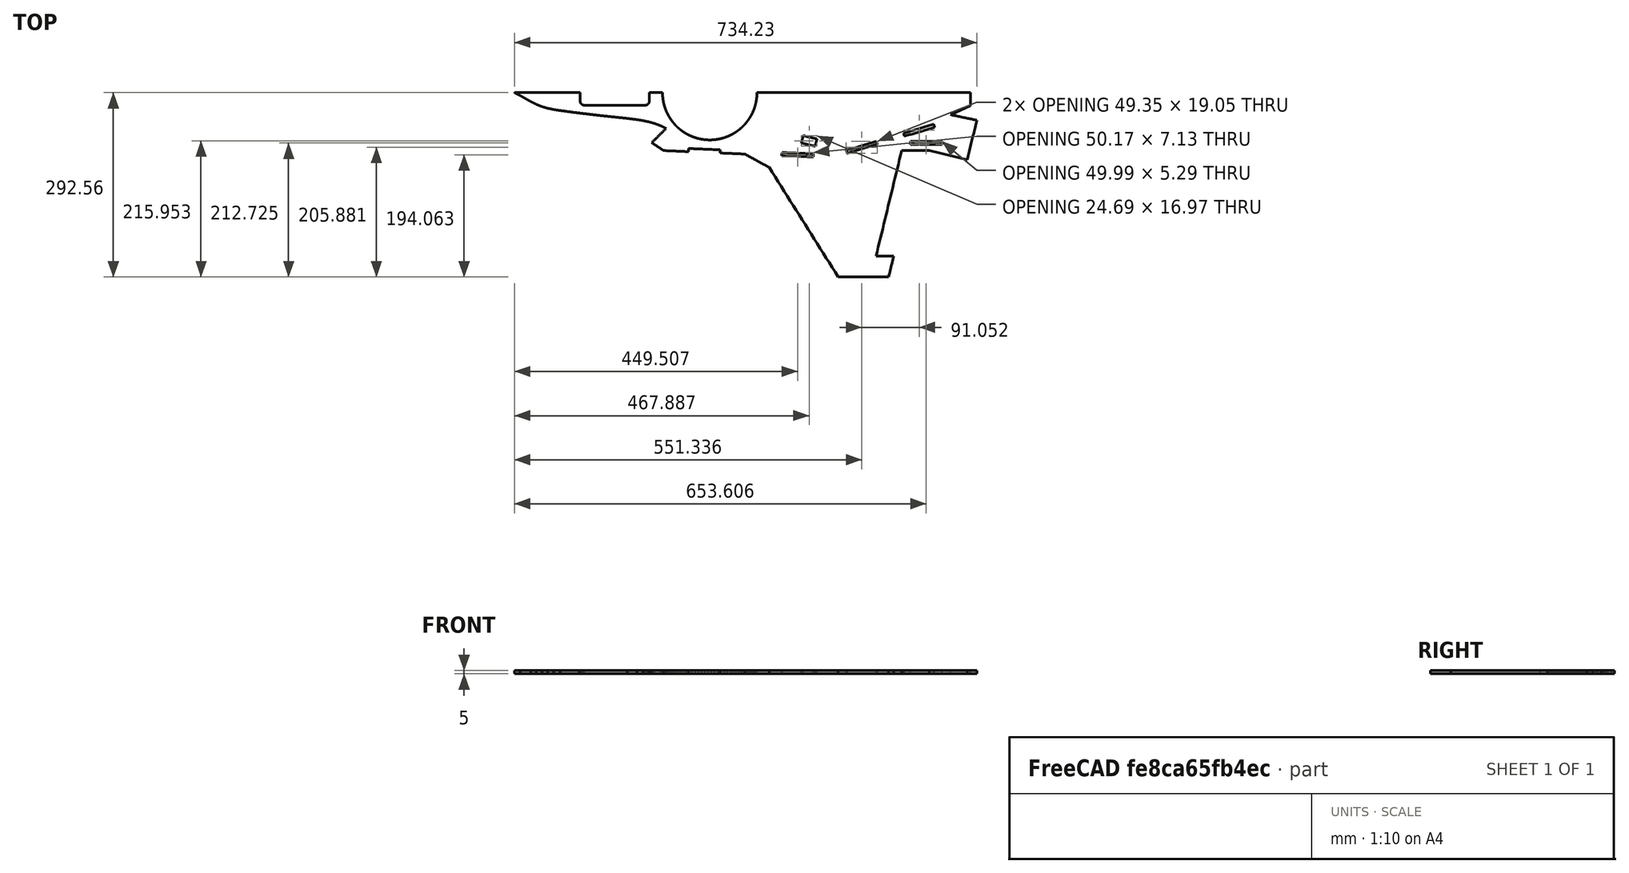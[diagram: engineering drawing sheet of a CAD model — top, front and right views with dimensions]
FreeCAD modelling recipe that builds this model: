
FCSTD DOCUMENT  (FreeCAD 0.19R)
Label: F-35_v2_parts_1
License: All rights reserved
LicenseURL: http://en.wikipedia.org/wiki/All_rights_reserved
objects: PartDesign::CoordinateSystem×8, App::DocumentObjectGroup×2, App::FeaturePython×1, Sketcher::SketchObject×1, PartDesign::Pad×1, PartDesign::Body×1, App::Part×1
note: 12 computed .brp shape members not serialized (recipe doc carries the construction recipe); baked Part::Feature solids carry a one-line shape summary decoded from their .brp

FEATURE [App::DocumentObjectGroup] Parts
FEATURE [PartDesign::CoordinateSystem] LCS_Origin
  AttacherType = Attacher::AttachEngine3D
  MapMode = 2
  Support = -> [X_Axis]
FEATURE [App::DocumentObjectGroup] Constraints
FEATURE [App::FeaturePython] Variables  # WARN: FeaturePython — macro-defined, semantics opaque (R4)
FEATURE [Sketcher::SketchObject] Sketch
  FullyConstrained = false
  sketch-geometry (125):
    g0: BSplineCurve PolesCount=2 KnotsCount=2 Degree=1 IsPeriodic=0
    g1: BSplineCurve PolesCount=2 KnotsCount=2 Degree=1 IsPeriodic=0
    g2: BSplineCurve PolesCount=2 KnotsCount=2 Degree=1 IsPeriodic=0
    g3: BSplineCurve PolesCount=2 KnotsCount=2 Degree=1 IsPeriodic=0
    g4: BSplineCurve PolesCount=2 KnotsCount=2 Degree=1 IsPeriodic=0
    g5: BSplineCurve PolesCount=2 KnotsCount=2 Degree=1 IsPeriodic=0
    g6: BSplineCurve PolesCount=2 KnotsCount=2 Degree=1 IsPeriodic=0
    g7: BSplineCurve PolesCount=2 KnotsCount=2 Degree=1 IsPeriodic=0
    g8: BSplineCurve PolesCount=2 KnotsCount=2 Degree=1 IsPeriodic=0
    g9: BSplineCurve PolesCount=2 KnotsCount=2 Degree=1 IsPeriodic=0
    g10: BSplineCurve PolesCount=2 KnotsCount=2 Degree=1 IsPeriodic=0
    g11: BSplineCurve PolesCount=2 KnotsCount=2 Degree=1 IsPeriodic=0
    g12: BSplineCurve PolesCount=2 KnotsCount=2 Degree=1 IsPeriodic=0
    g13: BSplineCurve PolesCount=2 KnotsCount=2 Degree=1 IsPeriodic=0
    g14: BSplineCurve PolesCount=2 KnotsCount=2 Degree=1 IsPeriodic=0
    g15: BSplineCurve PolesCount=2 KnotsCount=2 Degree=1 IsPeriodic=0
    g16: BSplineCurve PolesCount=2 KnotsCount=2 Degree=1 IsPeriodic=0
    g17: BSplineCurve PolesCount=2 KnotsCount=2 Degree=1 IsPeriodic=0
    g18: BSplineCurve PolesCount=2 KnotsCount=2 Degree=1 IsPeriodic=0
    g19: BSplineCurve PolesCount=2 KnotsCount=2 Degree=1 IsPeriodic=0
    g20: BSplineCurve PolesCount=2 KnotsCount=2 Degree=1 IsPeriodic=0
    g21: BSplineCurve PolesCount=2 KnotsCount=2 Degree=1 IsPeriodic=0
    g22: BSplineCurve PolesCount=2 KnotsCount=2 Degree=1 IsPeriodic=0
    g23: BSplineCurve PolesCount=2 KnotsCount=2 Degree=1 IsPeriodic=0
    g24: BSplineCurve PolesCount=2 KnotsCount=2 Degree=1 IsPeriodic=0
    g25: BSplineCurve PolesCount=2 KnotsCount=2 Degree=1 IsPeriodic=0
    g26: BSplineCurve PolesCount=2 KnotsCount=2 Degree=1 IsPeriodic=0
    g27: BSplineCurve PolesCount=2 KnotsCount=2 Degree=1 IsPeriodic=0
    g28: BSplineCurve PolesCount=2 KnotsCount=2 Degree=1 IsPeriodic=0
    g29: BSplineCurve PolesCount=2 KnotsCount=2 Degree=1 IsPeriodic=0
    g30: BSplineCurve PolesCount=2 KnotsCount=2 Degree=1 IsPeriodic=0
    g31: BSplineCurve PolesCount=2 KnotsCount=2 Degree=1 IsPeriodic=0
    g32: BSplineCurve PolesCount=2 KnotsCount=2 Degree=1 IsPeriodic=0
    g33: BSplineCurve PolesCount=2 KnotsCount=2 Degree=1 IsPeriodic=0
    g34: BSplineCurve PolesCount=2 KnotsCount=2 Degree=1 IsPeriodic=0
    g35: BSplineCurve PolesCount=2 KnotsCount=2 Degree=1 IsPeriodic=0
    g36: BSplineCurve PolesCount=2 KnotsCount=2 Degree=1 IsPeriodic=0
    g37: BSplineCurve PolesCount=2 KnotsCount=2 Degree=1 IsPeriodic=0
    g38: BSplineCurve PolesCount=2 KnotsCount=2 Degree=1 IsPeriodic=0
    g39: BSplineCurve PolesCount=2 KnotsCount=2 Degree=1 IsPeriodic=0
    g40: BSplineCurve PolesCount=2 KnotsCount=2 Degree=1 IsPeriodic=0
    g41: BSplineCurve PolesCount=2 KnotsCount=2 Degree=1 IsPeriodic=0
    g42: BSplineCurve PolesCount=2 KnotsCount=2 Degree=1 IsPeriodic=0
    g43: BSplineCurve PolesCount=2 KnotsCount=2 Degree=1 IsPeriodic=0
    g44: BSplineCurve PolesCount=2 KnotsCount=2 Degree=1 IsPeriodic=0
    g45: BSplineCurve PolesCount=2 KnotsCount=2 Degree=1 IsPeriodic=0
    g46: BSplineCurve PolesCount=2 KnotsCount=2 Degree=1 IsPeriodic=0
    g47: BSplineCurve PolesCount=2 KnotsCount=2 Degree=1 IsPeriodic=0
    g48: BSplineCurve PolesCount=2 KnotsCount=2 Degree=1 IsPeriodic=0
    g49: BSplineCurve PolesCount=2 KnotsCount=2 Degree=1 IsPeriodic=0
    g50: BSplineCurve PolesCount=2 KnotsCount=2 Degree=1 IsPeriodic=0
    g51: BSplineCurve PolesCount=2 KnotsCount=2 Degree=1 IsPeriodic=0
    g52: BSplineCurve PolesCount=2 KnotsCount=2 Degree=1 IsPeriodic=0
    g53: BSplineCurve PolesCount=2 KnotsCount=2 Degree=1 IsPeriodic=0
    g54: BSplineCurve PolesCount=2 KnotsCount=2 Degree=1 IsPeriodic=0
    g55: BSplineCurve PolesCount=2 KnotsCount=2 Degree=1 IsPeriodic=0
    g56: BSplineCurve PolesCount=2 KnotsCount=2 Degree=1 IsPeriodic=0
    g57: BSplineCurve PolesCount=2 KnotsCount=2 Degree=1 IsPeriodic=0
    g58: BSplineCurve PolesCount=2 KnotsCount=2 Degree=1 IsPeriodic=0
    g59: BSplineCurve PolesCount=2 KnotsCount=2 Degree=1 IsPeriodic=0
    g60: BSplineCurve PolesCount=2 KnotsCount=2 Degree=1 IsPeriodic=0
    g61: BSplineCurve PolesCount=2 KnotsCount=2 Degree=1 IsPeriodic=0
    g62: BSplineCurve PolesCount=2 KnotsCount=2 Degree=1 IsPeriodic=0
    g63: BSplineCurve PolesCount=2 KnotsCount=2 Degree=1 IsPeriodic=0
    g64: BSplineCurve PolesCount=2 KnotsCount=2 Degree=1 IsPeriodic=0
    g65: BSplineCurve PolesCount=2 KnotsCount=2 Degree=1 IsPeriodic=0
    g66: BSplineCurve PolesCount=2 KnotsCount=2 Degree=1 IsPeriodic=0
    g67: BSplineCurve PolesCount=2 KnotsCount=2 Degree=1 IsPeriodic=0
    g68: BSplineCurve PolesCount=2 KnotsCount=2 Degree=1 IsPeriodic=0
    g69: BSplineCurve PolesCount=2 KnotsCount=2 Degree=1 IsPeriodic=0
    g70: BSplineCurve PolesCount=2 KnotsCount=2 Degree=1 IsPeriodic=0
    g71: BSplineCurve PolesCount=2 KnotsCount=2 Degree=1 IsPeriodic=0
    g72: BSplineCurve PolesCount=2 KnotsCount=2 Degree=1 IsPeriodic=0
    g73: BSplineCurve PolesCount=2 KnotsCount=2 Degree=1 IsPeriodic=0
    g74: BSplineCurve PolesCount=2 KnotsCount=2 Degree=1 IsPeriodic=0
    g75: BSplineCurve PolesCount=2 KnotsCount=2 Degree=1 IsPeriodic=0
    g76: BSplineCurve PolesCount=2 KnotsCount=2 Degree=1 IsPeriodic=0
    g77: BSplineCurve PolesCount=2 KnotsCount=2 Degree=1 IsPeriodic=0
    g78: BSplineCurve PolesCount=2 KnotsCount=2 Degree=1 IsPeriodic=0
    g79: BSplineCurve PolesCount=2 KnotsCount=2 Degree=1 IsPeriodic=0
    g80: BSplineCurve PolesCount=2 KnotsCount=2 Degree=1 IsPeriodic=0
    g81: BSplineCurve PolesCount=2 KnotsCount=2 Degree=1 IsPeriodic=0
    g82: BSplineCurve PolesCount=2 KnotsCount=2 Degree=1 IsPeriodic=0
    g83: BSplineCurve PolesCount=2 KnotsCount=2 Degree=1 IsPeriodic=0
    g84: BSplineCurve PolesCount=2 KnotsCount=2 Degree=1 IsPeriodic=0
    g85: BSplineCurve PolesCount=2 KnotsCount=2 Degree=1 IsPeriodic=0
    g86: BSplineCurve PolesCount=2 KnotsCount=2 Degree=1 IsPeriodic=0
    g87: BSplineCurve PolesCount=2 KnotsCount=2 Degree=1 IsPeriodic=0
    g88: BSplineCurve PolesCount=2 KnotsCount=2 Degree=1 IsPeriodic=0
    g89: BSplineCurve PolesCount=2 KnotsCount=2 Degree=1 IsPeriodic=0
    g90: BSplineCurve PolesCount=2 KnotsCount=2 Degree=1 IsPeriodic=0
    g91: BSplineCurve PolesCount=2 KnotsCount=2 Degree=1 IsPeriodic=0
    g92: BSplineCurve PolesCount=2 KnotsCount=2 Degree=1 IsPeriodic=0
    g93: BSplineCurve PolesCount=2 KnotsCount=2 Degree=1 IsPeriodic=0
    g94: BSplineCurve PolesCount=2 KnotsCount=2 Degree=1 IsPeriodic=0
    g95: BSplineCurve PolesCount=2 KnotsCount=2 Degree=1 IsPeriodic=0
    g96: BSplineCurve PolesCount=2 KnotsCount=2 Degree=1 IsPeriodic=0
    g97: BSplineCurve PolesCount=2 KnotsCount=2 Degree=1 IsPeriodic=0
    g98: BSplineCurve PolesCount=2 KnotsCount=2 Degree=1 IsPeriodic=0
    g99: BSplineCurve PolesCount=2 KnotsCount=2 Degree=1 IsPeriodic=0
    g100: BSplineCurve PolesCount=2 KnotsCount=2 Degree=1 IsPeriodic=0
    g101: BSplineCurve PolesCount=2 KnotsCount=2 Degree=1 IsPeriodic=0
    g102: BSplineCurve PolesCount=2 KnotsCount=2 Degree=1 IsPeriodic=0
    g103: BSplineCurve PolesCount=2 KnotsCount=2 Degree=1 IsPeriodic=0
    g104: BSplineCurve PolesCount=2 KnotsCount=2 Degree=1 IsPeriodic=0
    g105: BSplineCurve PolesCount=2 KnotsCount=2 Degree=1 IsPeriodic=0
    g106: BSplineCurve PolesCount=2 KnotsCount=2 Degree=1 IsPeriodic=0
    g107: BSplineCurve PolesCount=2 KnotsCount=2 Degree=1 IsPeriodic=0
    g108: BSplineCurve PolesCount=2 KnotsCount=2 Degree=1 IsPeriodic=0
    g109: BSplineCurve PolesCount=2 KnotsCount=2 Degree=1 IsPeriodic=0
    g110: BSplineCurve PolesCount=2 KnotsCount=2 Degree=1 IsPeriodic=0
    g111: BSplineCurve PolesCount=2 KnotsCount=2 Degree=1 IsPeriodic=0
    g112: BSplineCurve PolesCount=2 KnotsCount=2 Degree=1 IsPeriodic=0
    g113: BSplineCurve PolesCount=2 KnotsCount=2 Degree=1 IsPeriodic=0
    g114: BSplineCurve PolesCount=2 KnotsCount=2 Degree=1 IsPeriodic=0
    g115: BSplineCurve PolesCount=2 KnotsCount=2 Degree=1 IsPeriodic=0
    g116: BSplineCurve PolesCount=2 KnotsCount=2 Degree=1 IsPeriodic=0
    g117: BSplineCurve PolesCount=2 KnotsCount=2 Degree=1 IsPeriodic=0
    g118: BSplineCurve PolesCount=2 KnotsCount=2 Degree=1 IsPeriodic=0
    g119: BSplineCurve PolesCount=2 KnotsCount=2 Degree=1 IsPeriodic=0
    g120: BSplineCurve PolesCount=2 KnotsCount=2 Degree=1 IsPeriodic=0
    g121: BSplineCurve PolesCount=2 KnotsCount=2 Degree=1 IsPeriodic=0
    g122: BSplineCurve PolesCount=2 KnotsCount=2 Degree=1 IsPeriodic=0
    g123: BSplineCurve PolesCount=2 KnotsCount=2 Degree=1 IsPeriodic=0
    g124: BSplineCurve PolesCount=2 KnotsCount=2 Degree=1 IsPeriodic=0
  constraints (76):
    c: Coincident(g20,g21)
    c: Coincident(g21,g22)
    c: Coincident(g22,g23)
    c: Coincident(g23,g24)
    c: Coincident(g24,g25)
    c: Coincident(g25,g26)
    c: Coincident(g26,g27)
    c: Coincident(g29,g30)
    c: Coincident(g30,g31)
    c: Coincident(g31,g32)
    c: Coincident(g32,g33)
    c: Coincident(g33,g34)
    c: Coincident(g34,g35)
    c: Coincident(g35,g36)
    c: Coincident(g39,g40)
    c: Coincident(g40,g41)
    c: Coincident(g41,g42)
    c: Coincident(g42,g43)
    c: Coincident(g43,g44)
    c: Coincident(g44,g45)
    c: Coincident(g45,g46)
    c: Coincident(g46,g47)
    c: Coincident(g47,g48)
    c: Coincident(g48,g49)
    c: Coincident(g49,g50)
    c: Coincident(g50,g51)
    c: Coincident(g51,g52)
    c: Coincident(g52,g53)
    c: Coincident(g53,g54)
    c: Coincident(g54,g55)
    c: Coincident(g55,g56)
    c: Coincident(g56,g57)
    c: Coincident(g57,g58)
    c: Coincident(g58,g59)
    c: Coincident(g59,g60)
    c: Coincident(g60,g61)
    c: Coincident(g61,g62)
    c: Coincident(g62,g63)
    c: Coincident(g63,g64)
    c: Coincident(g64,g65)
    c: Coincident(g65,g66)
    c: Coincident(g66,g67)
    c: Coincident(g67,g68)
    c: Coincident(g68,g69)
    c: Coincident(g69,g70)
    c: Coincident(g70,g71)
    c: Coincident(g71,g72)
    c: Coincident(g72,g73)
    c: Coincident(g73,g74)
    c: Coincident(g74,g75)
    c: Coincident(g75,g76)
    c: Coincident(g76,g77)
    c: Coincident(g77,g78)
    c: Coincident(g78,g79)
    c: Coincident(g79,g80)
    c: Coincident(g80,g81)
    c: Coincident(g81,g82)
    c: Coincident(g82,g83)
    c: Coincident(g103,g104)
    c: Coincident(g104,g105)
    c: Coincident(g105,g106)
    c: Coincident(g106,g107)
    c: Coincident(g107,g108)
    c: Coincident(g108,g109)
    c: Coincident(g109,g110)
    c: Coincident(g110,g111)
    c: Coincident(g111,g112)
    c: Coincident(g112,g113)
    c: Coincident(g113,g114)
    c: Coincident(g114,g115)
    c: Coincident(g115,g116)
    c: Coincident(g116,g117)
    c: Coincident(g117,g118)
    c: Coincident(g118,g119)
    c: Coincident(g119,g120)
    c: Coincident(g120,g121)
FEATURE [PartDesign::Pad] Pad
  Direction = (1,1,1)
  Length = 5
  Length2 = 100
  Profile = -> Sketch
  Type = 0
FEATURE [PartDesign::Body] Body  label="Part1"
  Group = -> [Sketch,Pad]
  Origin = -> Origin001
  Tip = -> Pad
FEATURE [PartDesign::CoordinateSystem] LCS_1
  AttacherType = Attacher::AttachEngine3D
  MapMode = 7
  Placement = pos=(856.063,-121.302,0) rot=(0,1,0;3.14159rad)
  Support = -> [Pad]
FEATURE [PartDesign::CoordinateSystem] LCS_2
  AttacherType = Attacher::AttachEngine3D
  MapMode = 7
  Placement = pos=(367.078,-121.302,0) rot=(0,1,0;3.14159rad)
  Support = -> [Pad]
FEATURE [PartDesign::CoordinateSystem] LCS_3
  AttacherType = Attacher::AttachEngine3D
  MapMode = 7
  Placement = pos=(408.529,-209.884,0) rot=(0.014931,0.707028,0.707028;3.11173rad)
  Support = -> [Pad]
FEATURE [PartDesign::CoordinateSystem] LCS_4
  AttacherType = Attacher::AttachEngine3D
  MapMode = 7
  Placement = pos=(658.719,-212.706,0) rot=(-0.101306,0.703469,0.703469;3.34352rad)
  Support = -> [Pad]
FEATURE [PartDesign::CoordinateSystem] LCS_6
  AttacherType = Attacher::AttachEngine3D
  MapMode = 7
  Placement = pos=(850.63,-227.699,5) rot=(0.985165,-0.121346,-0.121346;1.58574rad)
  Support = -> [Pad]
FEATURE [PartDesign::CoordinateSystem] LCS_5
  AttacherType = Attacher::AttachEngine3D
  MapMode = 7
  Placement = pos=(746.737,-213.2,5) rot=(0.084189,0.704596,0.704596;2.97361rad)
  Support = -> [Pad]
FEATURE [PartDesign::CoordinateSystem] LCS_7
  AttacherType = Attacher::AttachEngine3D
  MapMode = 45
  Placement = pos=(810.661,-201.276,2.5) rot=(0.707107,0,0.707107;3.14159rad)
  Support = -> [Pad]
FEATURE [App::Part] Model
  Configuration = 0
  Group = -> [LCS_Origin,Constraints,Variables,Body,LCS_1,LCS_2,LCS_3,LCS_4,LCS_6,LCS_5,LCS_7]
  Origin = -> Origin
  Type = Assembly4 Model
